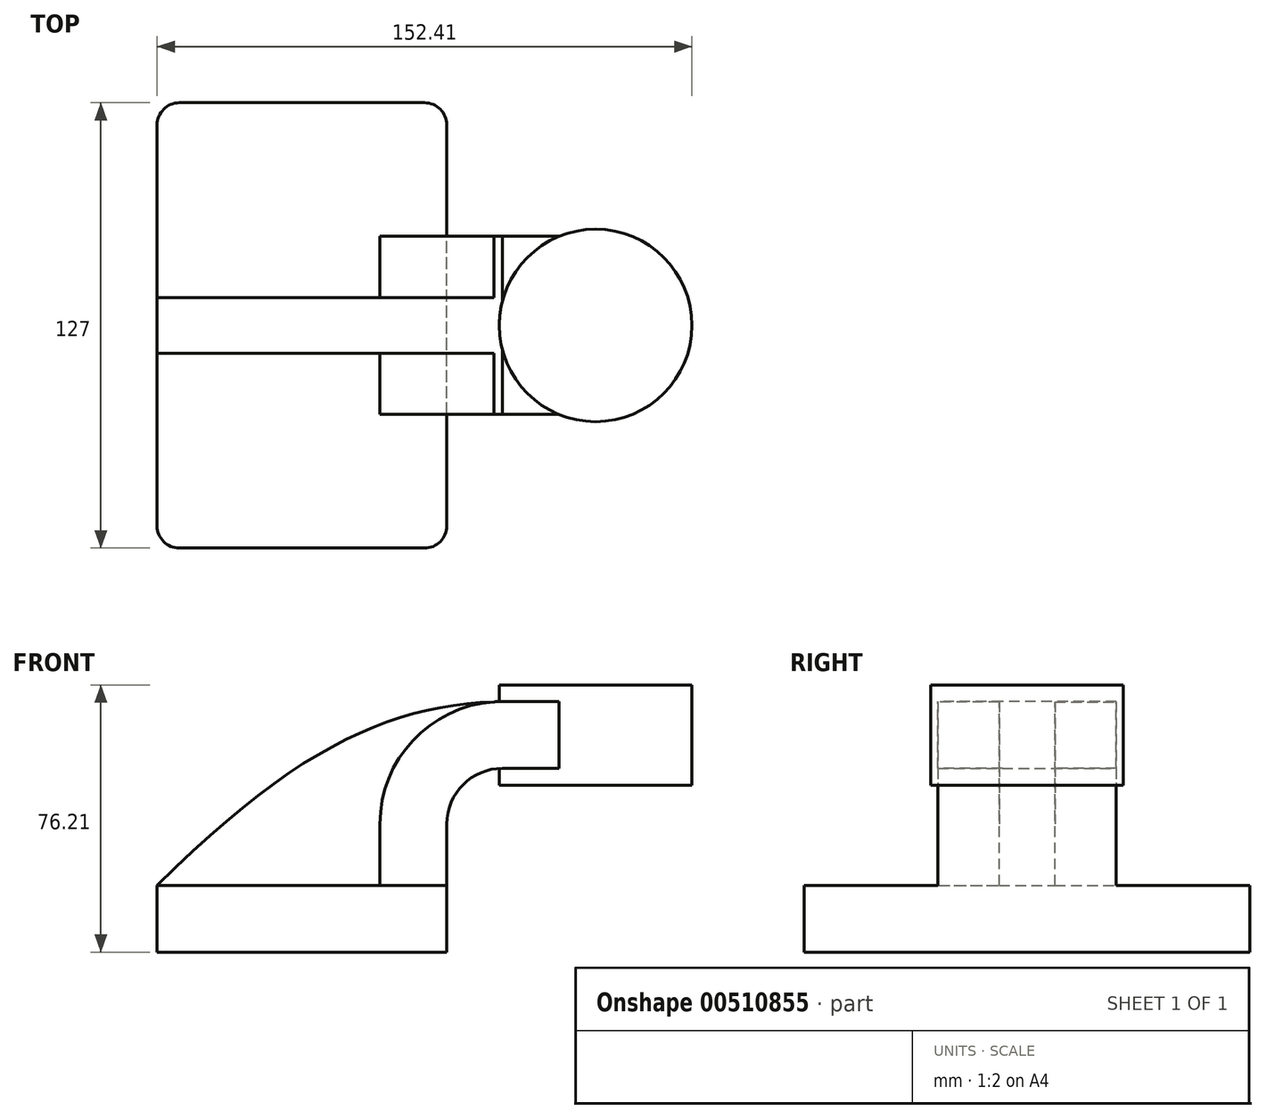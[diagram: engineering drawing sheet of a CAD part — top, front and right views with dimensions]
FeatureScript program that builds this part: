
annotation { "Feature Type Name" : "Feature", "Feature Type Description" : "" }
export const myFeature = defineFeature(function(context is Context, id is Id, definition is map)
    precondition{}
    {
        {
            var Q0;
            Q0=qCreatedBy(makeId("Front.planeOp"),FACE);
            var sketch = newSketch(context, id + "F0", { "sketchPlane" : qUnion([Q0])});
            skLineSegment(sketch, "E0.bottom", {"start": v(41.27, 9.53) * mm, "end": v(-41.28, 9.53) * mm});
            skLineSegment(sketch, "E0.top", {"start": v(41.28, -9.52) * mm, "end": v(-41.27, -9.52) * mm});
            skLineSegment(sketch, "E0.left", {"start": v(41.28, 9.53) * mm, "end": v(41.28, -9.52) * mm});
            skLineSegment(sketch, "E0.right", {"start": v(-41.28, 9.53) * mm, "end": v(-41.27, -9.52) * mm});
            skPoint(sketch, "E0.middle", {"position": v(0, 0) * mm});
            skLineSegment(sketch, "E1", {"start": v(41.27, 9.53) * mm, "end": v(41.27, 27) * mm});
            skArc(sketch, "E2", {"start": v(41.27, 27) * mm, "mid": v(45.92, 38.23) * mm, "end": v(57.15, 42.88) * mm});
            skLineSegment(sketch, "E3", {"start": v(57.15, 42.88) * mm, "end": v(83.68, 42.88) * mm});
            skLineSegment(sketch, "E4.bottom", {"start": v(60.32, 66.68) * mm, "end": v(111.13, 66.68) * mm});
            skLineSegment(sketch, "E4.top", {"start": v(60.32, 38.1) * mm, "end": v(111.13, 38.1) * mm});
            skLineSegment(sketch, "E4.left", {"start": v(60.33, 66.68) * mm, "end": v(60.33, 38.1) * mm});
            skLineSegment(sketch, "E4.right", {"start": v(111.13, 66.68) * mm, "end": v(111.13, 38.1) * mm});
            skLineSegment(sketch, "E5.0", {"start": v(57.15, 61.93) * mm, "end": v(83.68, 61.93) * mm});
            skArc(sketch, "E5.1", {"start": v(22.23, 27) * mm, "mid": v(32.45, 51.7) * mm, "end": v(57.15, 61.93) * mm});
            skLineSegment(sketch, "E5.2", {"start": v(22.22, 9.53) * mm, "end": v(22.22, 27) * mm});
            skFitSpline(sketch, "E6", {"points": [v(-41.28, 9.53) * mm, v(57.15, 61.93) * mm], "startDerivative": vector(123.83, 122.57) * mm, "endDerivative": vector(93, 2.48) * mm});
            skLineSegment(sketch, "E7", {"start": v(83.68, 66.68) * mm, "end": v(83.68, 38.1) * mm});
            skPoint(sketch, "E7.startSnap0", {"position": v(85.73, 66.68) * mm});
            skSolve(sketch);
        }
        {
            var Q0;
            Q0=makeQuery(id+"F0.imprint","IMPRINT",FACE,{"disambiguationData":[TD([[makeQuery(id+"F0.imprint","IMPRINT",EDGE,{"derivedFrom":sQuery(id+"F0.wireOp",EDGE,"E0.top")}),-1.0]])]});
            extrude(context, id + "F1", {"entities" : qUnion([Q0]), "endBound" : BoundingType.SYMMETRIC, "depth" : 127 * mm});
        }
        {
            var Q0;
            {var subQ9=sQuery(id+"F0.wireOp",EDGE,"E1");Q0=makeQuery(id+"F0.imprint","IMPRINT",FACE,{"disambiguationData":[TD([[makeQuery(id+"F0.imprint","IMPRINT",EDGE,{"derivedFrom":subQ9}),1.0]])]});}
            var Q1;
            {var subQ0=sQuery(id+"F0.wireOp",EDGE,"E7");var subQ1=sQuery(id+"F0.wireOp",EDGE,"E3");var subQ2=makeQuery(id+"F0.imprint","INTERSECT",VERTEX,{"derivedFrom":[subQ1,subQ0]});Q1=makeQuery(id+"F0.imprint","IMPRINT",FACE,{"disambiguationData":[TD([[makeQuery(id+"F0.imprint","IMPRINT",EDGE,{"disambiguationData":[TD([[subQ2,1.0]])],"derivedFrom":subQ1}),1.0]])]});}
            extrude(context, id + "F2", {"entities" : qUnion([Q0, Q1]), "operationType" : NewBodyOperationType.ADD, "endBound" : BoundingType.SYMMETRIC, "depth" : 50.8 * mm});
        }
        {
            var Q0;
            {var subQ3=sQuery(id+"F0.wireOp",EDGE,"E5.2");Q0=makeQuery(id+"F0.imprint","IMPRINT",FACE,{"disambiguationData":[TD([[makeQuery(id+"F0.imprint","IMPRINT",EDGE,{"derivedFrom":subQ3}),1.0]])]});}
            extrude(context, id + "F3", {"entities" : qUnion([Q0]), "operationType" : NewBodyOperationType.ADD, "endBound" : BoundingType.SYMMETRIC, "depth" : 15.88 * mm});
        }
        {
            var Q0;
            {var subQ4=sQuery(id+"F0.wireOp",EDGE,"E4.right");Q0=makeQuery(id+"F0.imprint","IMPRINT",FACE,{"disambiguationData":[TD([[makeQuery(id+"F0.imprint","IMPRINT",EDGE,{"derivedFrom":subQ4}),-1.0]])]});}
            var Q1;
            Q1=sQuery(id+"F0.wireOp",EDGE,"E7");
            revolve(context, id + "F4", {"operationType" : NewBodyOperationType.ADD, "entities" : qUnion([Q0]), "axis" : qUnion([Q1]), "revolveType" : RevolveType.FULL});
        }
        {
            var Q0;
            Q0=makeQuery(id+"F1.opExtrude","CAP_EDGE",EDGE,{"disambiguationData":[OSD([sQuery(id+"F0.wireOp",EDGE,"E0.right")])],"isStart":false});
            var Q1;
            Q1=makeQuery(id+"F1.opExtrude","CAP_EDGE",EDGE,{"disambiguationData":[OSD([sQuery(id+"F0.wireOp",EDGE,"E0.left")])],"isStart":false});
            var Q2;
            Q2=makeQuery(id+"F1.opExtrude","CAP_EDGE",EDGE,{"disambiguationData":[OSD([sQuery(id+"F0.wireOp",EDGE,"E0.left")])],"isStart":true});
            var Q3;
            Q3=makeQuery(id+"F1.opExtrude","CAP_EDGE",EDGE,{"disambiguationData":[OSD([sQuery(id+"F0.wireOp",EDGE,"E0.right")])],"isStart":true});
            fillet(context, id + "F5", {"entities" : qUnion([Q0, Q1, Q2, Q3]), "radius" : 6.35 * mm, "tangentPropagation" : true, "allowEdgeOverflow" : false});
        }
    });
